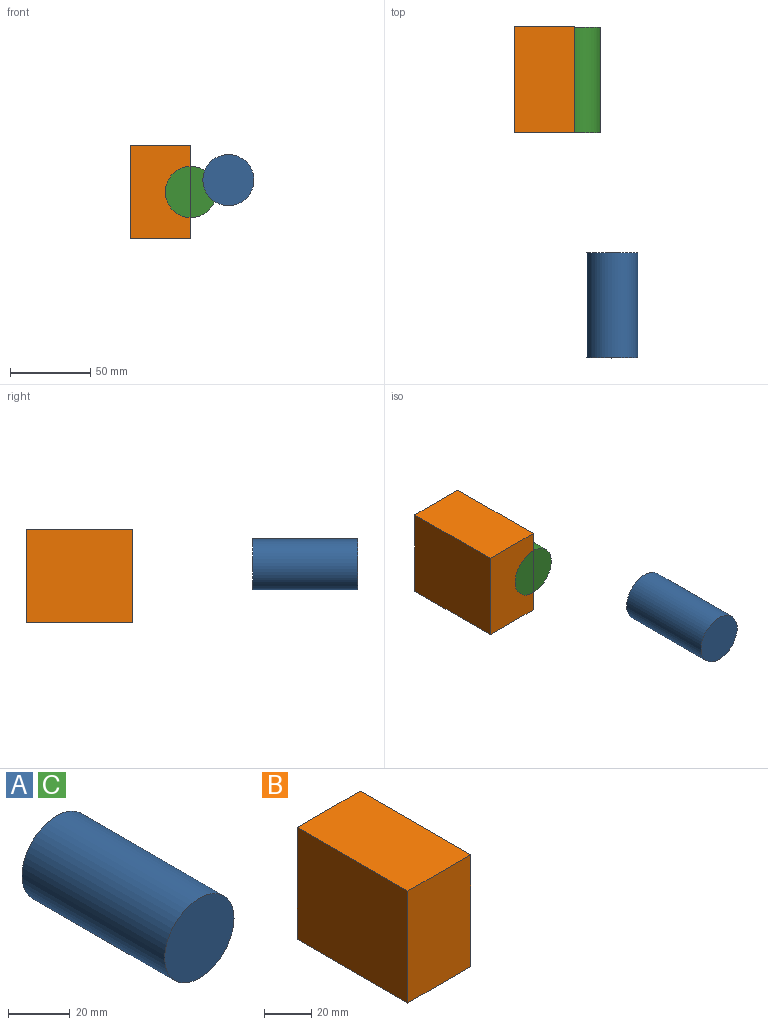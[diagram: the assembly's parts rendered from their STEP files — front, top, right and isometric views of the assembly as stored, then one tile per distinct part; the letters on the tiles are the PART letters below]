
ASSEMBLY  parts=3 mates=1
PART A: 3 faces, bbox 31.8x65.5x31.8 mm
  f0: cylinder r=15.9mm len=65.53mm, axis (0,1,0), area 6546.4mm2, adj f1,f2
  f1: plane 31.8x31.8mm, normal (0,-1,0), area 794.1mm2, adj f0
  f2: plane 31.8x31.8mm, normal (0,1,0), area 794.1mm2, adj f0
PART B: 6 faces, bbox 37.8x66.3x58.2 mm
  f0: plane 66.29x58.16mm, normal (-1,0,0), area 3855.8mm2, adj f1,f3,f4,f5
  f1: plane 66.29x37.81mm, normal (0,0,-1), area 2506.3mm2, adj f0,f2,f4,f5
  f2: plane 66.29x58.16mm, normal (1,0,0), area 3855.8mm2, adj f1,f3,f4,f5
  f3: plane 66.29x37.81mm, normal (0,0,1), area 2506.3mm2, adj f0,f2,f4,f5
  f4: plane 58.16x37.81mm, normal (0,1,0), area 2198.8mm2, adj f0,f1,f2,f3
  f5: plane 58.16x37.81mm, normal (0,-1,0), area 2198.8mm2, adj f0,f1,f2,f3
PART C: same geometry as A
PLACE A t=(-69.32,-117.92,-60.88)mm
PLACE B t=(-77.28,23.02,-11.86)mm
PLACE C t=(-92.7,22.24,-68.28)mm
MATE slider C.f0 <-> B.f5  axis (0,1,0) through (-99.38,22.24,-17.18)mm
